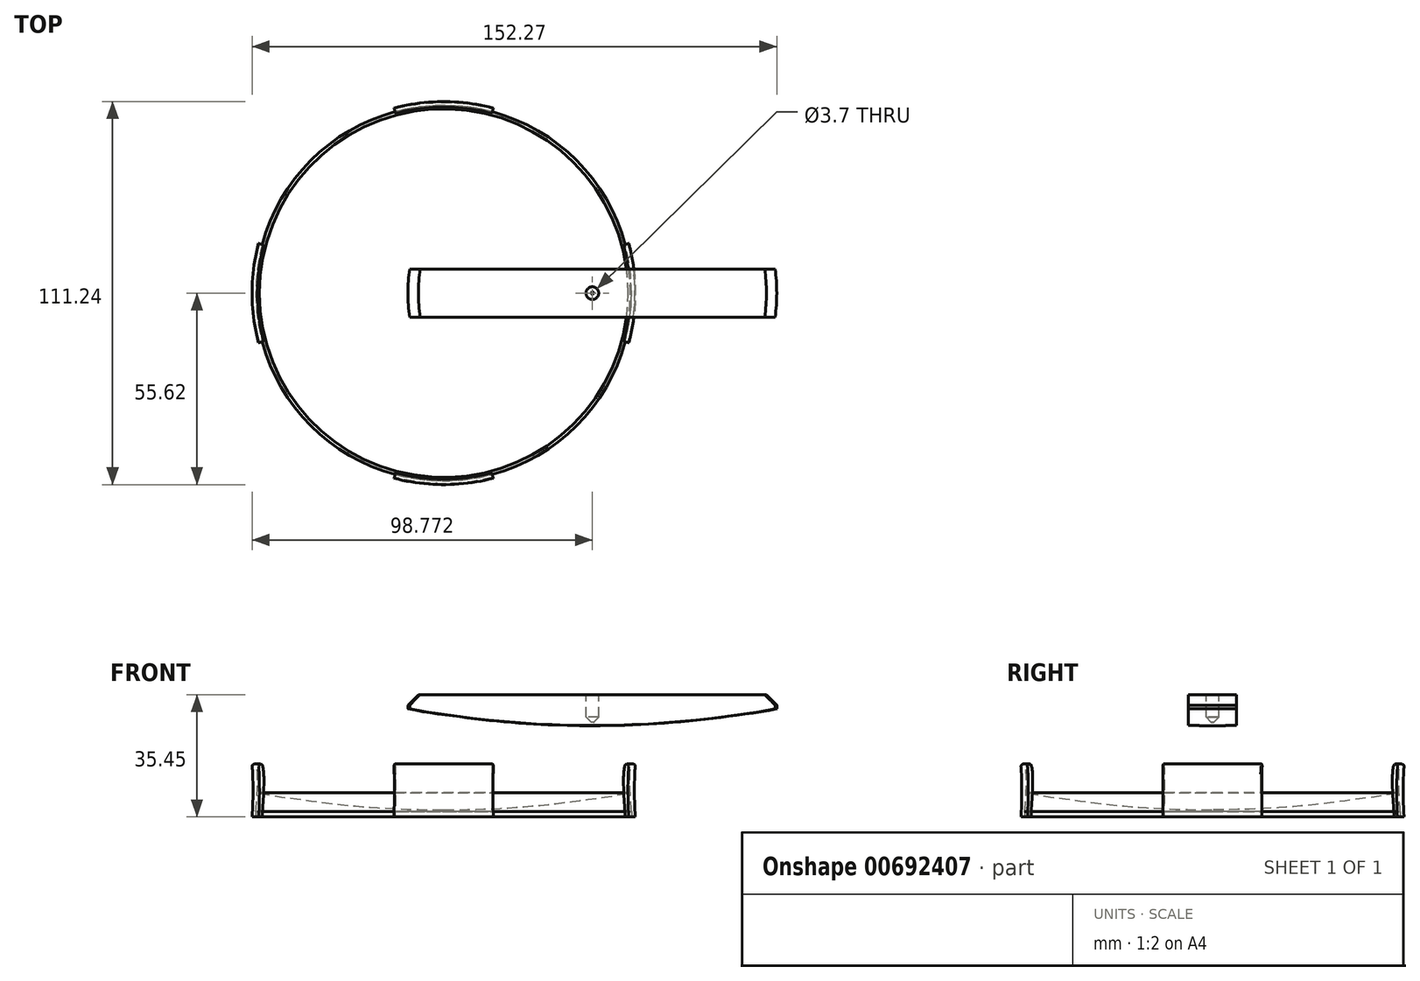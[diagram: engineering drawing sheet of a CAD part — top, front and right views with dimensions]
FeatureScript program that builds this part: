
annotation { "Feature Type Name" : "Feature", "Feature Type Description" : "" }
export const myFeature = defineFeature(function(context is Context, id is Id, definition is map)
    precondition{}
    {
        {
            var Q0;
            Q0=qCreatedBy(makeId("Front.planeOp"),FACE);
            var sketch = newSketch(context, id + "F0", { "sketchPlane" : qUnion([Q0])});
            skLineSegment(sketch, "E0.right", {"start": v(53.5, 0) * mm, "end": v(53.5, 5) * mm});
            skPoint(sketch, "E1", {"position": v(10.7, 0.2) * mm});
            skPoint(sketch, "E2", {"position": v(21.4, 0.8) * mm});
            skPoint(sketch, "E3", {"position": v(32.1, 1.8) * mm});
            skPoint(sketch, "E4", {"position": v(42.8, 3.2) * mm});
            skFitSpline(sketch, "E5", {"points": [v(0, 0) * mm, v(10.7, 0.2) * mm, v(21.4, 0.8) * mm, v(32.1, 1.8) * mm, v(42.8, 3.2) * mm, v(53.5, 5) * mm], "startDerivative": vector(50.32, 0.82) * mm, "endDerivative": vector(49.48, 13.06) * mm});
            skLineSegment(sketch, "E6.left", {"start": v(53.5, 0) * mm, "end": v(53.5, -2) * mm});
            skLineSegment(sketch, "E7", {"start": v(0, -2) * mm, "end": v(53.5, -2) * mm});
            skLineSegment(sketch, "E8", {"start": v(0, 0) * mm, "end": v(0, -2) * mm});
            skLineSegment(sketch, "E9", {"start": v(0, 14.47) * mm, "end": v(0, -8.17) * mm, "construction": true});
            skSolve(sketch);
        }
        {
            var Q0;
            Q0=makeQuery(id+"F0.imprint","IMPRINT",FACE,{"disambiguationData":[TD([[makeQuery(id+"F0.imprint","IMPRINT",EDGE,{"derivedFrom":sQuery(id+"F0.wireOp",EDGE,"E0.right")}),1.0]])]});
            var Q1;
            Q1=sQuery(id+"F0.wireOp",EDGE,"E9");
            revolve(context, id + "F1", {"entities" : qUnion([Q0]), "axis" : qUnion([Q1]), "revolveType" : RevolveType.FULL});
        }
        {
            var Q0;
            Q0=qCreatedBy(makeId("Right.planeOp"),FACE);
            var sketch = newSketch(context, id + "F2", { "sketchPlane" : qUnion([Q0])});
            skLineSegment(sketch, "E10.bottom", {"start": v(-54.5, -2) * mm, "end": v(-53.5, -2) * mm});
            skLineSegment(sketch, "E10.top", {"start": v(-54.5, -0.5) * mm, "end": v(-53.5, -0.5) * mm});
            skLineSegment(sketch, "E10.left", {"start": v(-54.5, -2) * mm, "end": v(-54.5, -0.5) * mm});
            skLineSegment(sketch, "E10.right", {"start": v(-53.5, -2) * mm, "end": v(-53.5, -0.5) * mm});
            skSolve(sketch);
        }
        {
            var Q0;
            Q0=makeQuery(id+"F2.imprint","IMPRINT",FACE,{"disambiguationData":[TD([[makeQuery(id+"F2.imprint","IMPRINT",EDGE,{"derivedFrom":sQuery(id+"F2.wireOp",EDGE,"E10.bottom")}),1.0]])]});
            var Q1;
            Q1=makeQuery(id+"F1.opRevolve","SWEPT_EDGE",EDGE,{"disambiguationData":[OSD([sQuery(id+"F0.wireOp",EDGE,"E6.left"),sQuery(id+"F0.wireOp",EDGE,"E7")])]});
            revolve(context, id + "F3", {"operationType" : NewBodyOperationType.ADD, "entities" : qUnion([Q0]), "axis" : qUnion([Q1]), "revolveType" : RevolveType.FULL});
        }
        {
            var Q0;
            Q0=qCreatedBy(makeId("Right.planeOp"),FACE);
            var sketch = newSketch(context, id + "F4", { "sketchPlane" : qUnion([Q0])});
            skLineSegment(sketch, "E11", {"start": v(-54.5, -0.5) * mm, "end": v(-54.5, -2.02) * mm});
            skLineSegment(sketch, "E12", {"start": v(-54.5, -2.02) * mm, "end": v(-55.56, -2.02) * mm});
            skFitSpline(sketch, "E13", {"points": [v(-55.56, -2.02) * mm, v(-55.58, 12.46) * mm, v(-55.56, 12.9) * mm, v(-54.82, 13.32) * mm, v(-54.5, -0.5) * mm], "startDerivative": vector(2.8, 47.76) * mm, "endDerivative": vector(-4.5, -49.68) * mm});
            skSolve(sketch);
        }
        {
            var Q0;
            Q0=makeQuery(id+"F4.imprint","IMPRINT",FACE,{"disambiguationData":[TD([[makeQuery(id+"F4.imprint","IMPRINT",EDGE,{"derivedFrom":sQuery(id+"F4.wireOp",EDGE,"E11")}),-1.0]])]});
            var Q1;
            Q1=makeQuery(id+"F1.opRevolve","SWEPT_EDGE",EDGE,{"disambiguationData":[OSD([sQuery(id+"F0.wireOp",EDGE,"E0.right"),sQuery(id+"F0.wireOp",EDGE,"E5")])]});
            revolve(context, id + "F5", {"entities" : qUnion([Q0]), "axis" : qUnion([Q1]), "revolveType" : RevolveType.SYMMETRIC, "angle" : 30 * degree});
        }
        {
            var Q0;
            Q0=makeQuery(id+"F5.opRevolve","SWEPT_BODY",BODY,{"disambiguationData":[OSD([sQuery(id+"F4.wireOp",EDGE,"E11"),sQuery(id+"F4.wireOp",EDGE,"E12"),sQuery(id+"F4.wireOp",EDGE,"E13")])]});
            var Q1;
            Q1=makeQuery(id+"F1.opRevolve","SWEPT_EDGE",EDGE,{"disambiguationData":[OSD([sQuery(id+"F0.wireOp",EDGE,"E0.right"),sQuery(id+"F0.wireOp",EDGE,"E5")])]});
            circularPattern(context, id + "F6", {"entities" : qUnion([Q0]), "axis" : qUnion([Q1]), "angle" : 360 * degree, "instanceCount" : 4, "equalSpace" : true});
        }
        {
            var Q0;
            Q0=qCreatedBy(makeId("Front.planeOp"),FACE);
            var sketch = newSketch(context, id + "F7", { "sketchPlane" : qUnion([Q0])});
            skFitSpline(sketch, "E14", {"points": [v(43.15, 24.43) * mm, v(53.85, 24.63) * mm, v(64.55, 25.23) * mm, v(75.25, 26.23) * mm, v(85.95, 27.63) * mm, v(96.65, 29.43) * mm], "startDerivative": vector(50.32, 0.82) * mm, "endDerivative": vector(49.48, 13.06) * mm});
            skLineSegment(sketch, "E15", {"start": v(96.65, 29.43) * mm, "end": v(96.65, 30.43) * mm});
            skLineSegment(sketch, "E16", {"start": v(43.15, 24.43) * mm, "end": v(43.15, 30.43) * mm});
            skLineSegment(sketch, "E17", {"start": v(43.15, 24.43) * mm, "end": v(43.15, 38.33) * mm, "construction": true});
            skLineSegment(sketch, "E18", {"start": v(43.15, 30.43) * mm, "end": v(43.15, 33.43) * mm});
            skLineSegment(sketch, "E19", {"start": v(43.15, 33.43) * mm, "end": v(93.65, 33.43) * mm});
            skLineSegment(sketch, "E20", {"start": v(93.65, 33.43) * mm, "end": v(96.65, 30.43) * mm});
            skSolve(sketch);
        }
        {
            var Q0;
            Q0=makeQuery(id+"F7.imprint","IMPRINT",FACE,{"disambiguationData":[TD([[makeQuery(id+"F7.imprint","IMPRINT",EDGE,{"derivedFrom":sQuery(id+"F7.wireOp",EDGE,"E14")}),1.0]])]});
            var Q1;
            Q1=sQuery(id+"F7.wireOp",EDGE,"E17");
            revolve(context, id + "F8", {"entities" : qUnion([Q0]), "axis" : qUnion([Q1]), "revolveType" : RevolveType.FULL});
        }
        {
            var Q0;
            Q0=makeQuery(id+"F8.opRevolve","SWEPT_FACE",FACE,{"disambiguationData":[OSD([sQuery(id+"F7.wireOp",EDGE,"E19")])]});
            var sketch = newSketch(context, id + "F9", { "sketchPlane" : qUnion([Q0])});
            skCircle(sketch, "E21", {"center": v(43.15, 0) * mm, "radius": 1.85 * mm});
            skSolve(sketch);
        }
        {
            var Q0;
            Q0 = qSketchRegion(id + "F9", true);
            extrude(context, id + "F10", {"entities" : qUnion([Q0]), "operationType" : NewBodyOperationType.REMOVE, "oppositeDirection" : true, "depth" : 8 * mm, "offsetDistance" : 25 * mm});
        }
        {
            var Q0;
            Q0=makeQuery(id+"F10.boolean.opBoolean","COPY",EDGE,{"derivedFrom":makeQuery(id+"F10.opExtrude","CAP_EDGE",EDGE,{"disambiguationData":[OSD([sQuery(id+"F9.wireOp",EDGE,"E21")])],"isStart":false})});
            chamfer(context, id + "F11", {"entities" : qUnion([Q0]), "width" : 1.5 * mm, "tangentPropagation" : true});
        }
        {
            var Q0;
            Q0=qCreatedBy(makeId("Front.planeOp"),FACE);
            cPlane(context, id + "F12", {"entities" : qUnion([Q0]), "cplaneType" : CPlaneType.OFFSET, "offset" : 7 * mm, "width" : 150 * mm, "height" : 150 * mm});
        }
        {
            var Q0;
            Q0=qCreatedBy(id+"F12.planeOp",FACE);
            var sketch = newSketch(context, id + "F13", { "sketchPlane" : qUnion([Q0])});
            skLineSegment(sketch, "E22.bottom", {"start": v(-14.3, 38.9) * mm, "end": v(99.38, 38.9) * mm});
            skLineSegment(sketch, "E22.top", {"start": v(-14.3, 20.2) * mm, "end": v(99.38, 20.2) * mm});
            skLineSegment(sketch, "E22.left", {"start": v(-14.3, 38.9) * mm, "end": v(-14.3, 20.2) * mm});
            skLineSegment(sketch, "E22.right", {"start": v(99.38, 38.9) * mm, "end": v(99.38, 20.2) * mm});
            skSolve(sketch);
        }
        {
            var Q0;
            Q0 = qSketchRegion(id + "F13", true);
            extrude(context, id + "F14", {"entities" : qUnion([Q0]), "operationType" : NewBodyOperationType.REMOVE, "depth" : 50 * mm, "offsetDistance" : 25 * mm});
        }
        {
            var Q0;
            Q0=qCreatedBy(makeId("Front.planeOp"),FACE);
            cPlane(context, id + "F15", {"entities" : qUnion([Q0]), "cplaneType" : CPlaneType.OFFSET, "offset" : 7 * mm, "oppositeDirection" : true, "width" : 150 * mm, "height" : 150 * mm});
        }
        {
            var Q0;
            Q0=qCreatedBy(id+"F15.planeOp",FACE);
            var sketch = newSketch(context, id + "F16", { "sketchPlane" : qUnion([Q0])});
            skLineSegment(sketch, "E23.bottom", {"start": v(103.12, 39.5) * mm, "end": v(-13.9, 39.5) * mm});
            skLineSegment(sketch, "E23.top", {"start": v(103.12, 18.81) * mm, "end": v(-13.9, 18.81) * mm});
            skLineSegment(sketch, "E23.left", {"start": v(103.12, 39.5) * mm, "end": v(103.12, 18.81) * mm});
            skLineSegment(sketch, "E23.right", {"start": v(-13.9, 39.5) * mm, "end": v(-13.9, 18.81) * mm});
            skSolve(sketch);
        }
        {
            var Q0;
            Q0 = qSketchRegion(id + "F16", true);
            extrude(context, id + "F17", {"entities" : qUnion([Q0]), "operationType" : NewBodyOperationType.REMOVE, "oppositeDirection" : true, "depth" : 50 * mm, "offsetDistance" : 25 * mm});
        }
    });
